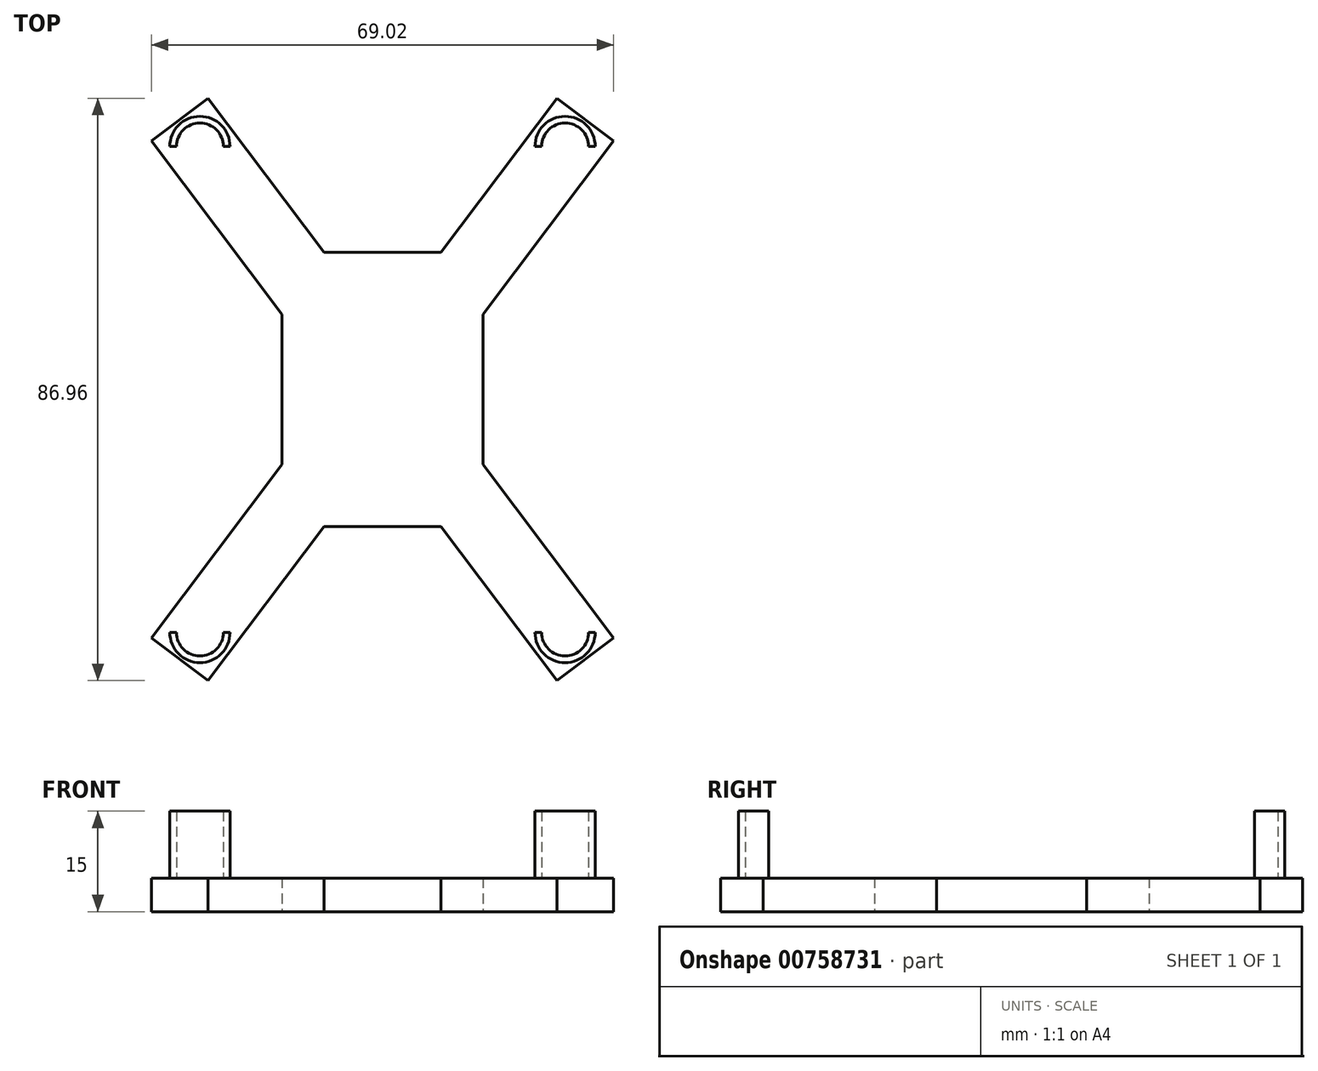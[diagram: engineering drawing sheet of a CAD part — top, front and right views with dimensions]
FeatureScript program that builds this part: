
annotation { "Feature Type Name" : "Feature", "Feature Type Description" : "" }
export const myFeature = defineFeature(function(context is Context, id is Id, definition is map)
    precondition{}
    {
        {
            var Q0;
            Q0=qCreatedBy(makeId("Top.planeOp"),FACE);
            var sketch = newSketch(context, id + "F0", { "sketchPlane" : qUnion([Q0])});
            skLineSegment(sketch, "E0.bottom", {"start": v(15, 20.5) * mm, "end": v(-15, 20.5) * mm});
            skLineSegment(sketch, "E0.top", {"start": v(15, -20.5) * mm, "end": v(-15, -20.5) * mm});
            skLineSegment(sketch, "E0.left", {"start": v(15, 20.5) * mm, "end": v(15, -20.5) * mm});
            skLineSegment(sketch, "E0.right", {"start": v(-15, 20.5) * mm, "end": v(-15, -20.5) * mm});
            skPoint(sketch, "E0.middle", {"position": v(0, 0) * mm});
            skLineSegment(sketch, "E1", {"start": v(26.04, 43.48) * mm, "end": v(8.74, 20.5) * mm});
            skLineSegment(sketch, "E2", {"start": v(34.51, 37.1) * mm, "end": v(15, 11.19) * mm});
            skLineSegment(sketch, "E3", {"start": v(26.04, 43.48) * mm, "end": v(34.51, 37.1) * mm});
            skLineSegment(sketch, "E4", {"start": v(0, 0) * mm, "end": v(-2.75, 0) * mm});
            skLineSegment(sketch, "E5", {"start": v(0, 0) * mm, "end": v(0, 2.4) * mm});
            skLineSegment(sketch, "E6.MirrorCS", {"start": v(-34.51, 37.1) * mm, "end": v(-15, 11.19) * mm});
            skLineSegment(sketch, "E7.MirrorCS", {"start": v(-26.04, 43.48) * mm, "end": v(-8.74, 20.5) * mm});
            skLineSegment(sketch, "E8.MirrorCS", {"start": v(-26.04, 43.48) * mm, "end": v(-34.51, 37.1) * mm});
            skLineSegment(sketch, "E9.MirrorCS", {"start": v(-34.51, -37.1) * mm, "end": v(-15, -11.19) * mm});
            skLineSegment(sketch, "E10.MirrorCS", {"start": v(-26.04, -43.48) * mm, "end": v(-8.74, -20.5) * mm});
            skLineSegment(sketch, "E11.MirrorCS", {"start": v(26.04, -43.48) * mm, "end": v(8.74, -20.5) * mm});
            skLineSegment(sketch, "E12.MirrorCS", {"start": v(34.51, -37.1) * mm, "end": v(15, -11.19) * mm});
            skLineSegment(sketch, "E13.MirrorCS", {"start": v(26.04, -43.48) * mm, "end": v(34.51, -37.1) * mm});
            skLineSegment(sketch, "E14.MirrorCS", {"start": v(-26.04, -43.48) * mm, "end": v(-34.51, -37.1) * mm});
            skSolve(sketch);
        }
        {
            var Q0;
            Q0 = qSketchRegion(id + "F0", true);
            extrude(context, id + "F1", {"entities" : qUnion([Q0]), "depth" : 5 * mm, "offsetDistance" : 25 * mm});
        }
        {
            var Q0;
            Q0=makeQuery(id+"F1.opExtrude","CAP_FACE",FACE,{"disambiguationData":[OSD([sQuery(id+"F0.wireOp",EDGE,"E0.bottom"),sQuery(id+"F0.wireOp",EDGE,"E0.top"),sQuery(id+"F0.wireOp",EDGE,"E0.left"),sQuery(id+"F0.wireOp",EDGE,"E0.right"),sQuery(id+"F0.wireOp",EDGE,"E1"),sQuery(id+"F0.wireOp",EDGE,"E2"),sQuery(id+"F0.wireOp",EDGE,"E3"),sQuery(id+"F0.wireOp",EDGE,"070567df-8bef-4a32-9086-5dec1096ebb70.MirrorCS"),sQuery(id+"F0.wireOp",EDGE,"eaa3fa47-ee3f-4150-88c3-2ea589e78a4e0.MirrorCS"),sQuery(id+"F0.wireOp",EDGE,"c91a21a2-5d18-4aa2-9e19-43bd840b31870.MirrorCS"),sQuery(id+"F0.wireOp",EDGE,"e926119c-a12f-4cba-9c68-f24ad0d1ed650.MirrorCS"),sQuery(id+"F0.wireOp",EDGE,"d50b6afb-b7e4-47c7-bf47-3d1312aff3230.MirrorCS"),sQuery(id+"F0.wireOp",EDGE,"8d3a2311-7c49-48f9-a340-80bb4853a81f0.MirrorCS"),sQuery(id+"F0.wireOp",EDGE,"67220796-e8a4-44f3-8922-260e74f4f7210.MirrorCS"),sQuery(id+"F0.wireOp",EDGE,"fcef7fca-2aaa-4716-bd70-f8582556729b0.MirrorCS"),sQuery(id+"F0.wireOp",EDGE,"679b465a-8a55-4cd7-8bee-8c5751aa6dbf0.MirrorCS")])],"isStart":false});
            var sketch = newSketch(context, id + "F2", { "sketchPlane" : qUnion([Q0])});
            skLineSegment(sketch, "E15", {"start": v(0, 0) * mm, "end": v(-2.54, 0) * mm});
            skLineSegment(sketch, "E16", {"start": v(0, 0) * mm, "end": v(-30.28, 40.3) * mm});
            skLineSegment(sketch, "E17", {"start": v(-30.28, 40.3) * mm, "end": v(-27.27, 36.3) * mm});
            skCircle(sketch, "E18", {"center": v(-27.27, 36.3) * mm, "radius": 3.5 * mm});
            skCircle(sketch, "E19.0", {"center": v(-27.27, 36.3) * mm, "radius": 4.5 * mm});
            skLineSegment(sketch, "E20", {"start": v(-23.77, 36.3) * mm, "end": v(-22.77, 36.3) * mm});
            skLineSegment(sketch, "E21", {"start": v(-30.77, 36.3) * mm, "end": v(-31.77, 36.3) * mm});
            skLineSegment(sketch, "E22", {"start": v(0, 0) * mm, "end": v(0, 4.5) * mm});
            skLineSegment(sketch, "E23.MirrorCS", {"start": v(30.77, 36.3) * mm, "end": v(31.77, 36.3) * mm});
            skLineSegment(sketch, "E24.MirrorCS", {"start": v(30.28, 40.3) * mm, "end": v(27.27, 36.3) * mm});
            skLineSegment(sketch, "E25.MirrorCS", {"start": v(23.77, 36.3) * mm, "end": v(22.77, 36.3) * mm});
            skCircle(sketch, "E26.MirrorC", {"center": v(27.27, 36.3) * mm, "radius": 3.5 * mm});
            skCircle(sketch, "E27.MirrorC", {"center": v(27.27, 36.3) * mm, "radius": 4.5 * mm});
            skLineSegment(sketch, "E28.MirrorCS", {"start": v(30.77, -36.3) * mm, "end": v(31.77, -36.3) * mm});
            skLineSegment(sketch, "E29.MirrorCS", {"start": v(23.77, -36.3) * mm, "end": v(22.77, -36.3) * mm});
            skLineSegment(sketch, "E30.MirrorCS", {"start": v(-30.77, -36.3) * mm, "end": v(-31.77, -36.3) * mm});
            skLineSegment(sketch, "E31.MirrorCS", {"start": v(-23.77, -36.3) * mm, "end": v(-22.77, -36.3) * mm});
            skLineSegment(sketch, "E32.MirrorCS", {"start": v(30.28, -40.3) * mm, "end": v(27.27, -36.3) * mm});
            skCircle(sketch, "E33.MirrorC", {"center": v(27.27, -36.3) * mm, "radius": 3.5 * mm});
            skCircle(sketch, "E34.MirrorC", {"center": v(-27.27, -36.3) * mm, "radius": 4.5 * mm});
            skCircle(sketch, "E35.MirrorC", {"center": v(-27.27, -36.3) * mm, "radius": 3.5 * mm});
            skLineSegment(sketch, "E36.MirrorCS", {"start": v(-30.28, -40.3) * mm, "end": v(-27.27, -36.3) * mm});
            skCircle(sketch, "E37.MirrorC", {"center": v(27.27, -36.3) * mm, "radius": 4.5 * mm});
            skSolve(sketch);
        }
        {
            var Q0;
            {var subQ5=sQuery(id+"F2.wireOp",EDGE,"E20");Q0=makeQuery(id+"F2.imprint","IMPRINT",FACE,{"disambiguationData":[TD([[makeQuery(id+"F2.imprint","IMPRINT",EDGE,{"derivedFrom":subQ5}),1.0]])]});}
            var Q1;
            {var subQ0=sQuery(id+"F2.wireOp",EDGE,"E23.MirrorCS");Q1=makeQuery(id+"F2.imprint","IMPRINT",FACE,{"disambiguationData":[TD([[makeQuery(id+"F2.imprint","IMPRINT",EDGE,{"derivedFrom":subQ0}),1.0]])]});}
            var Q2;
            {var subQ0=sQuery(id+"F2.wireOp",EDGE,"E25.MirrorCS");Q2=makeQuery(id+"F2.imprint","IMPRINT",FACE,{"disambiguationData":[TD([[makeQuery(id+"F2.imprint","IMPRINT",EDGE,{"derivedFrom":subQ0}),-1.0]])]});}
            var Q3;
            {var subQ0=sQuery(id+"F2.wireOp",EDGE,"E29.MirrorCS");Q3=makeQuery(id+"F2.imprint","IMPRINT",FACE,{"disambiguationData":[TD([[makeQuery(id+"F2.imprint","IMPRINT",EDGE,{"derivedFrom":subQ0}),1.0]])]});}
            var Q4;
            {var subQ0=sQuery(id+"F2.wireOp",EDGE,"E28.MirrorCS");Q4=makeQuery(id+"F2.imprint","IMPRINT",FACE,{"disambiguationData":[TD([[makeQuery(id+"F2.imprint","IMPRINT",EDGE,{"derivedFrom":subQ0}),-1.0]])]});}
            var Q5;
            {var subQ0=sQuery(id+"F2.wireOp",EDGE,"E30.MirrorCS");Q5=makeQuery(id+"F2.imprint","IMPRINT",FACE,{"disambiguationData":[TD([[makeQuery(id+"F2.imprint","IMPRINT",EDGE,{"derivedFrom":subQ0}),1.0]])]});}
            var Q6;
            {var subQ0=sQuery(id+"F2.wireOp",EDGE,"E31.MirrorCS");Q6=makeQuery(id+"F2.imprint","IMPRINT",FACE,{"disambiguationData":[TD([[makeQuery(id+"F2.imprint","IMPRINT",EDGE,{"derivedFrom":subQ0}),-1.0]])]});}
            var Q7;
            {var subQ5=sQuery(id+"F2.wireOp",EDGE,"E21");Q7=makeQuery(id+"F2.imprint","IMPRINT",FACE,{"disambiguationData":[TD([[makeQuery(id+"F2.imprint","IMPRINT",EDGE,{"derivedFrom":subQ5}),-1.0]])]});}
            extrude(context, id + "F3", {"entities" : qUnion([Q0, Q1, Q2, Q3, Q4, Q5, Q6, Q7]), "operationType" : NewBodyOperationType.ADD, "depth" : 10 * mm, "offsetDistance" : 25 * mm});
        }
    });
